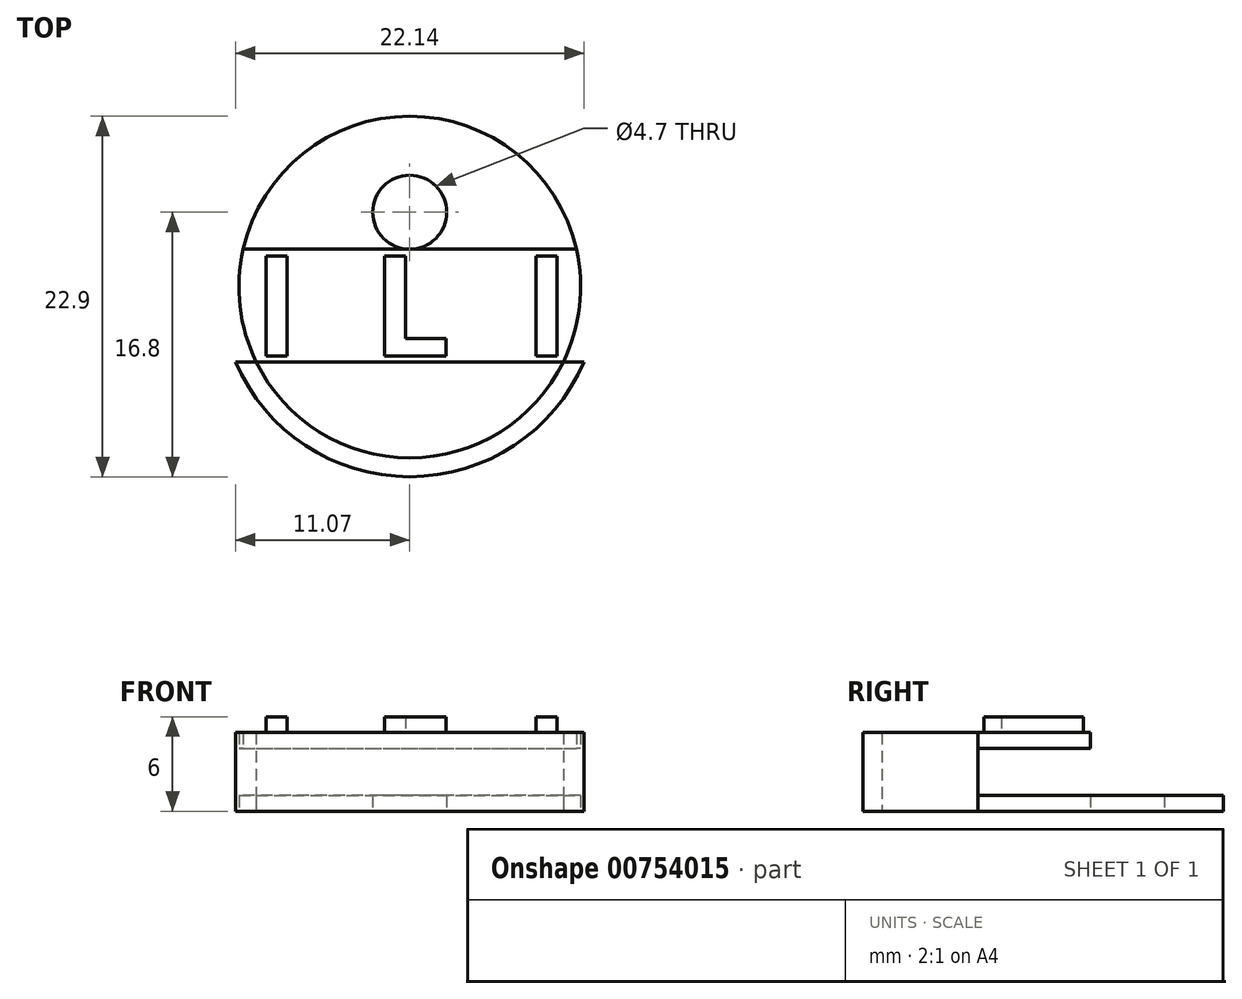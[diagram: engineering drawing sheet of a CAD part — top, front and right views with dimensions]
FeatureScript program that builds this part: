
annotation { "Feature Type Name" : "Feature", "Feature Type Description" : "" }
export const myFeature = defineFeature(function(context is Context, id is Id, definition is map)
    precondition{}
    {
        {
            var Q0;
            Q0=qCreatedBy(makeId("Top.planeOp"),FACE);
            var sketch = newSketch(context, id + "F0", { "sketchPlane" : qUnion([Q0])});
            skCircle(sketch, "E0", {"center": v(0, 0) * mm, "radius": 12.05 * mm});
            skLineSegment(sketch, "E1", {"start": v(-11.07, -4.75) * mm, "end": v(11.07, -4.75) * mm});
            skCircle(sketch, "E2", {"center": v(0, 4.75) * mm, "radius": 2.35 * mm});
            skCircle(sketch, "E3", {"center": v(0, 0) * mm, "radius": 10.85 * mm});
            skLineSegment(sketch, "E4", {"start": v(0, 2.4) * mm, "end": v(-10.58, 2.4) * mm});
            skLineSegment(sketch, "E5", {"start": v(0, 2.4) * mm, "end": v(10.58, 2.4) * mm});
            skText(sketch, "E6", { "text": "I  L  I", "fontName": "OpenSans-Bold.ttf"});
            const initialGuessF0  = {"E6": [-0.00993, -0.00437, 1, 0, 0.00638]};
            skSetInitialGuess(sketch, initialGuessF0);
            skSolve(sketch);
        }
        {
            var Q0;
            {var subQ0=sQuery(id+"F0.wireOp",EDGE,"E4");Q0=makeQuery(id+"F0.imprint","IMPRINT",FACE,{"disambiguationData":[TD([[makeQuery(id+"F0.imprint","IMPRINT",EDGE,{"derivedFrom":subQ0}),1.0]])]});}
            var Q1;
            {var subQ0=sQuery(id+"F0.wireOp",EDGE,"E1");var subQ1=sQuery(id+"F0.wireOp",EDGE,"E0");var subQ5=makeQuery(id+"F0.imprint","INTERSECT",VERTEX,{"disambiguationData":[OD(0.0)],"derivedFrom":[subQ1,subQ0]});Q1=makeQuery(id+"F0.imprint","IMPRINT",FACE,{"disambiguationData":[TD([[makeQuery(id+"F0.imprint","IMPRINT",EDGE,{"disambiguationData":[TD([[subQ5,1.0]])],"derivedFrom":subQ1}),1.0]])]});}
            var Q2;
            Q2=makeQuery(id+"F0.imprint","IMPRINT",FACE,{"disambiguationData":[TD([[makeQuery(id+"F0.imprint","IMPRINT",EDGE,{"derivedFrom":sQuery(id+"F0.wireOp",EDGE,"3db4fb92-41e3-4f33-b393-5101edaef4c4.sketch_text.stroke-59")}),1.0]])]});
            var Q3;
            {var subQ0=sQuery(id+"F0.wireOp",EDGE,"3db4fb92-41e3-4f33-b393-5101edaef4c4.sketch_text.stroke-5");Q3=makeQuery(id+"F0.imprint","IMPRINT",FACE,{"disambiguationData":[TD([[makeQuery(id+"F0.imprint","IMPRINT",EDGE,{"derivedFrom":subQ0}),1.0]])]});}
            extrude(context, id + "F1", {"entities" : qUnion([Q0, Q1, Q2, Q3]), "depth" : 5 * mm, "offsetDistance" : 25 * mm});
        }
        {
            var Q0;
            Q0=makeQuery(id+"F0.imprint","IMPRINT",FACE,{"disambiguationData":[TD([[makeQuery(id+"F0.imprint","IMPRINT",EDGE,{"derivedFrom":sQuery(id+"F0.wireOp",EDGE,"E6.sketch_text.stroke-0")}),-1.0]])]});
            var Q1;
            Q1=makeQuery(id+"F0.imprint","IMPRINT",FACE,{"disambiguationData":[TD([[makeQuery(id+"F0.imprint","IMPRINT",EDGE,{"derivedFrom":sQuery(id+"F0.wireOp",EDGE,"E6.sketch_text.stroke-4")}),-1.0]])]});
            var Q2;
            Q2=makeQuery(id+"F0.imprint","IMPRINT",FACE,{"disambiguationData":[TD([[makeQuery(id+"F0.imprint","IMPRINT",EDGE,{"derivedFrom":sQuery(id+"F0.wireOp",EDGE,"E6.sketch_text.stroke-10")}),-1.0]])]});
            extrude(context, id + "F2", {"entities" : qUnion([Q0, Q1, Q2]), "operationType" : NewBodyOperationType.ADD, "depth" : 6 * mm, "offsetDistance" : 25 * mm});
        }
        {
            var Q0;
            {var subQ0=sQuery(id+"F0.wireOp",EDGE,"E4");Q0=makeQuery(id+"F0.imprint","IMPRINT",FACE,{"disambiguationData":[TD([[makeQuery(id+"F0.imprint","IMPRINT",EDGE,{"derivedFrom":subQ0}),1.0]])]});}
            var Q1;
            Q1=makeQuery(id+"F0.imprint","IMPRINT",FACE,{"disambiguationData":[TD([[makeQuery(id+"F0.imprint","IMPRINT",EDGE,{"derivedFrom":sQuery(id+"F0.wireOp",EDGE,"3db4fb92-41e3-4f33-b393-5101edaef4c4.sketch_text.stroke-0")}),-1.0]])]});
            var Q2;
            Q2=makeQuery(id+"F0.imprint","IMPRINT",FACE,{"disambiguationData":[TD([[makeQuery(id+"F0.imprint","IMPRINT",EDGE,{"derivedFrom":sQuery(id+"F0.wireOp",EDGE,"3db4fb92-41e3-4f33-b393-5101edaef4c4.sketch_text.stroke-28")}),-1.0]])]});
            var Q3;
            Q3=makeQuery(id+"F0.imprint","IMPRINT",FACE,{"disambiguationData":[TD([[makeQuery(id+"F0.imprint","IMPRINT",EDGE,{"derivedFrom":sQuery(id+"F0.wireOp",EDGE,"3db4fb92-41e3-4f33-b393-5101edaef4c4.sketch_text.stroke-41")}),-1.0]])]});
            var Q4;
            Q4=makeQuery(id+"F0.imprint","IMPRINT",FACE,{"disambiguationData":[TD([[makeQuery(id+"F0.imprint","IMPRINT",EDGE,{"derivedFrom":sQuery(id+"F0.wireOp",EDGE,"3db4fb92-41e3-4f33-b393-5101edaef4c4.sketch_text.stroke-47")}),-1.0]])]});
            var Q5;
            Q5=makeQuery(id+"F0.imprint","IMPRINT",FACE,{"disambiguationData":[TD([[makeQuery(id+"F0.imprint","IMPRINT",EDGE,{"derivedFrom":sQuery(id+"F0.wireOp",EDGE,"3db4fb92-41e3-4f33-b393-5101edaef4c4.sketch_text.stroke-59")}),-1.0]])]});
            var Q6;
            Q6=makeQuery(id+"F0.imprint","IMPRINT",FACE,{"disambiguationData":[TD([[makeQuery(id+"F0.imprint","IMPRINT",EDGE,{"derivedFrom":sQuery(id+"F0.wireOp",EDGE,"3db4fb92-41e3-4f33-b393-5101edaef4c4.sketch_text.stroke-59")}),1.0]])]});
            var Q7;
            {var subQ0=sQuery(id+"F0.wireOp",EDGE,"3db4fb92-41e3-4f33-b393-5101edaef4c4.sketch_text.stroke-5");Q7=makeQuery(id+"F0.imprint","IMPRINT",FACE,{"disambiguationData":[TD([[makeQuery(id+"F0.imprint","IMPRINT",EDGE,{"derivedFrom":subQ0}),1.0]])]});}
            var Q8;
            Q8=makeQuery(id+"F0.imprint","IMPRINT",FACE,{"disambiguationData":[TD([[makeQuery(id+"F0.imprint","IMPRINT",EDGE,{"derivedFrom":sQuery(id+"F0.wireOp",EDGE,"fc78e92f-c637-4d0b-ac51-c9f91acad043.sketch_text.stroke-0")}),-1.0]])]});
            var Q9;
            Q9=makeQuery(id+"F0.imprint","IMPRINT",FACE,{"disambiguationData":[TD([[makeQuery(id+"F0.imprint","IMPRINT",EDGE,{"derivedFrom":sQuery(id+"F0.wireOp",EDGE,"E6.sketch_text.stroke-0")}),-1.0]])]});
            var Q10;
            Q10=makeQuery(id+"F0.imprint","IMPRINT",FACE,{"disambiguationData":[TD([[makeQuery(id+"F0.imprint","IMPRINT",EDGE,{"derivedFrom":sQuery(id+"F0.wireOp",EDGE,"E6.sketch_text.stroke-4")}),-1.0]])]});
            var Q11;
            Q11=makeQuery(id+"F0.imprint","IMPRINT",FACE,{"disambiguationData":[TD([[makeQuery(id+"F0.imprint","IMPRINT",EDGE,{"derivedFrom":sQuery(id+"F0.wireOp",EDGE,"E6.sketch_text.stroke-10")}),-1.0]])]});
            extrude(context, id + "F3", {"entities" : qUnion([Q0, Q1, Q2, Q3, Q4, Q5, Q6, Q7, Q8, Q9, Q10, Q11]), "operationType" : NewBodyOperationType.REMOVE, "depth" : 4 * mm, "offsetDistance" : 25 * mm});
        }
        {
            var Q0;
            Q0=makeQuery(id+"F0.imprint","IMPRINT",FACE,{"disambiguationData":[TD([[makeQuery(id+"F0.imprint","IMPRINT",EDGE,{"derivedFrom":sQuery(id+"F0.wireOp",EDGE,"E2")}),-1.0]])]});
            var Q1;
            {var subQ0=sQuery(id+"F0.wireOp",EDGE,"E4");Q1=makeQuery(id+"F0.imprint","IMPRINT",FACE,{"disambiguationData":[TD([[makeQuery(id+"F0.imprint","IMPRINT",EDGE,{"derivedFrom":subQ0}),1.0]])]});}
            var Q2;
            Q2=makeQuery(id+"F0.imprint","IMPRINT",FACE,{"disambiguationData":[TD([[makeQuery(id+"F0.imprint","IMPRINT",EDGE,{"derivedFrom":sQuery(id+"F0.wireOp",EDGE,"3db4fb92-41e3-4f33-b393-5101edaef4c4.sketch_text.stroke-0")}),-1.0]])]});
            var Q3;
            Q3=makeQuery(id+"F0.imprint","IMPRINT",FACE,{"disambiguationData":[TD([[makeQuery(id+"F0.imprint","IMPRINT",EDGE,{"derivedFrom":sQuery(id+"F0.wireOp",EDGE,"3db4fb92-41e3-4f33-b393-5101edaef4c4.sketch_text.stroke-28")}),-1.0]])]});
            var Q4;
            Q4=makeQuery(id+"F0.imprint","IMPRINT",FACE,{"disambiguationData":[TD([[makeQuery(id+"F0.imprint","IMPRINT",EDGE,{"derivedFrom":sQuery(id+"F0.wireOp",EDGE,"3db4fb92-41e3-4f33-b393-5101edaef4c4.sketch_text.stroke-41")}),-1.0]])]});
            var Q5;
            Q5=makeQuery(id+"F0.imprint","IMPRINT",FACE,{"disambiguationData":[TD([[makeQuery(id+"F0.imprint","IMPRINT",EDGE,{"derivedFrom":sQuery(id+"F0.wireOp",EDGE,"3db4fb92-41e3-4f33-b393-5101edaef4c4.sketch_text.stroke-47")}),-1.0]])]});
            var Q6;
            Q6=makeQuery(id+"F0.imprint","IMPRINT",FACE,{"disambiguationData":[TD([[makeQuery(id+"F0.imprint","IMPRINT",EDGE,{"derivedFrom":sQuery(id+"F0.wireOp",EDGE,"3db4fb92-41e3-4f33-b393-5101edaef4c4.sketch_text.stroke-59")}),-1.0]])]});
            var Q7;
            Q7=makeQuery(id+"F0.imprint","IMPRINT",FACE,{"disambiguationData":[TD([[makeQuery(id+"F0.imprint","IMPRINT",EDGE,{"derivedFrom":sQuery(id+"F0.wireOp",EDGE,"3db4fb92-41e3-4f33-b393-5101edaef4c4.sketch_text.stroke-59")}),1.0]])]});
            var Q8;
            {var subQ0=sQuery(id+"F0.wireOp",EDGE,"3db4fb92-41e3-4f33-b393-5101edaef4c4.sketch_text.stroke-5");Q8=makeQuery(id+"F0.imprint","IMPRINT",FACE,{"disambiguationData":[TD([[makeQuery(id+"F0.imprint","IMPRINT",EDGE,{"derivedFrom":subQ0}),1.0]])]});}
            var Q9;
            Q9=makeQuery(id+"F0.imprint","IMPRINT",FACE,{"disambiguationData":[TD([[makeQuery(id+"F0.imprint","IMPRINT",EDGE,{"derivedFrom":sQuery(id+"F0.wireOp",EDGE,"fc78e92f-c637-4d0b-ac51-c9f91acad043.sketch_text.stroke-0")}),-1.0]])]});
            var Q10;
            Q10=makeQuery(id+"F0.imprint","IMPRINT",FACE,{"disambiguationData":[TD([[makeQuery(id+"F0.imprint","IMPRINT",EDGE,{"derivedFrom":sQuery(id+"F0.wireOp",EDGE,"E6.sketch_text.stroke-0")}),-1.0]])]});
            var Q11;
            Q11=makeQuery(id+"F0.imprint","IMPRINT",FACE,{"disambiguationData":[TD([[makeQuery(id+"F0.imprint","IMPRINT",EDGE,{"derivedFrom":sQuery(id+"F0.wireOp",EDGE,"E6.sketch_text.stroke-4")}),-1.0]])]});
            var Q12;
            Q12=makeQuery(id+"F0.imprint","IMPRINT",FACE,{"disambiguationData":[TD([[makeQuery(id+"F0.imprint","IMPRINT",EDGE,{"derivedFrom":sQuery(id+"F0.wireOp",EDGE,"E6.sketch_text.stroke-10")}),-1.0]])]});
            extrude(context, id + "F4", {"entities" : qUnion([Q0, Q1, Q2, Q3, Q4, Q5, Q6, Q7, Q8, Q9, Q10, Q11, Q12]), "operationType" : NewBodyOperationType.ADD, "depth" : 1 * mm, "offsetDistance" : 25 * mm});
        }
    });
